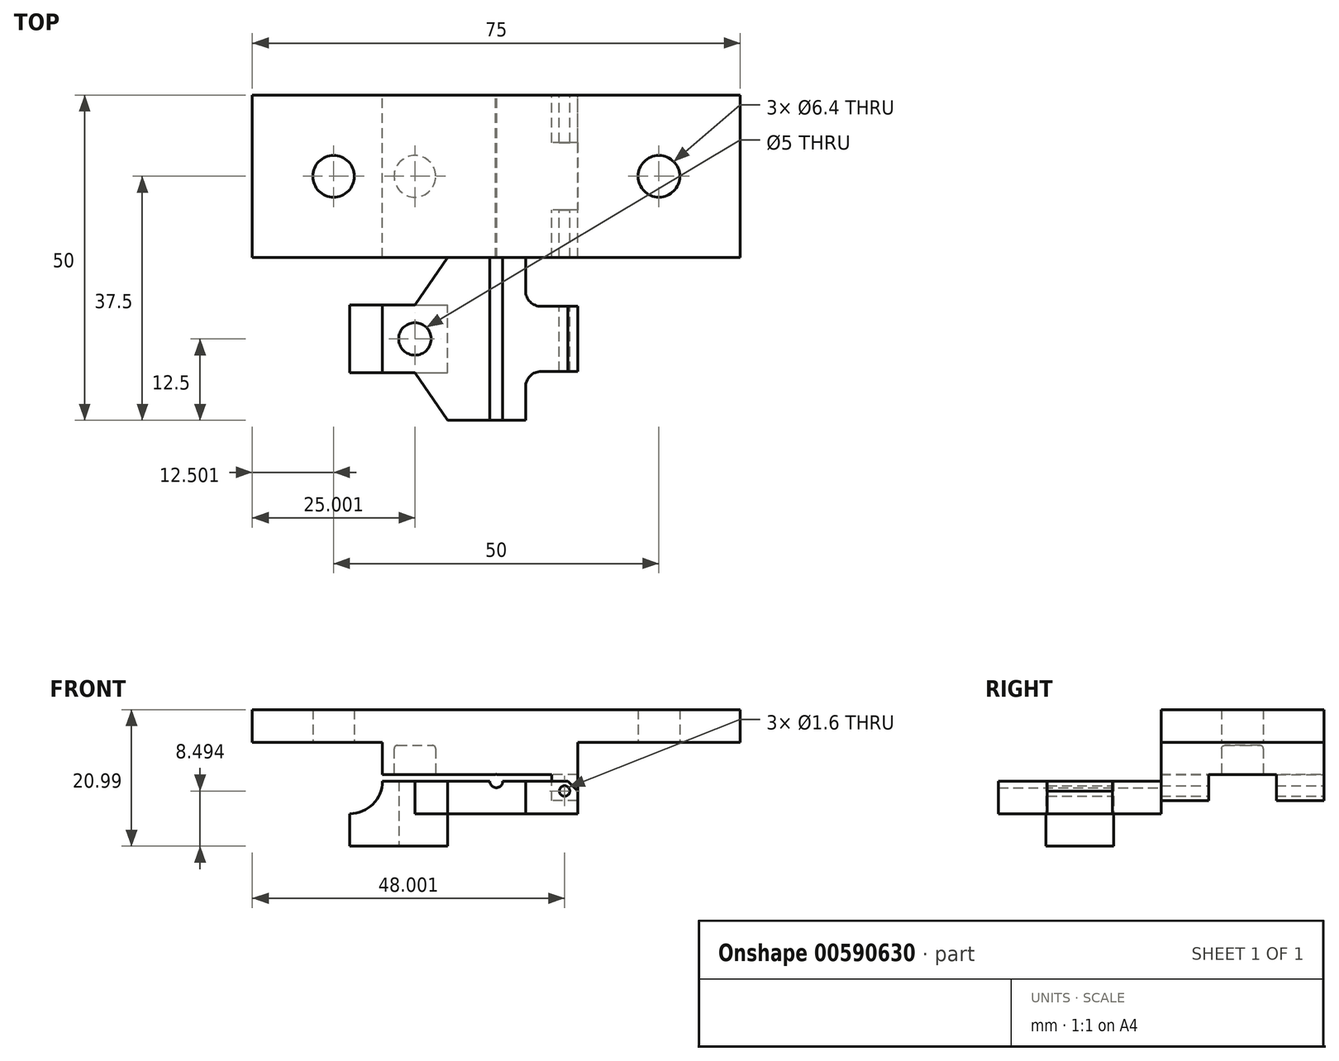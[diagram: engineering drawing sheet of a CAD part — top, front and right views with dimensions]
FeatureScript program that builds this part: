
annotation { "Feature Type Name" : "Feature", "Feature Type Description" : "" }
export const myFeature = defineFeature(function(context is Context, id is Id, definition is map)
    precondition{}
    {
        {
            var Q0;
            Q0=qCreatedBy(makeId("Front.planeOp"),FACE);
            var sketch = newSketch(context, id + "F0", { "sketchPlane" : qUnion([Q0])});
            skLineSegment(sketch, "E0", {"start": v(14.18, -10.49) * mm, "end": v(5.79, -10.49) * mm});
            skLineSegment(sketch, "E1", {"start": v(5.79, -10.49) * mm, "end": v(5.7, -10.4) * mm});
            skArc(sketch, "E2", {"start": v(5.7, -10.4) * mm, "mid": v(5.68, -10.4) * mm, "end": v(5.66, -10.4) * mm});
            skLineSegment(sketch, "E3", {"start": v(5.66, -10.4) * mm, "end": v(5.57, -10.49) * mm});
            skLineSegment(sketch, "E4", {"start": v(5.57, -10.49) * mm, "end": v(-11.82, -10.49) * mm});
            skLineSegment(sketch, "E5", {"start": v(-11.82, -10.49) * mm, "end": v(-11.82, -5.49) * mm});
            skLineSegment(sketch, "E6", {"start": v(-11.82, -5.49) * mm, "end": v(18.18, -5.49) * mm});
            skLineSegment(sketch, "E7", {"start": v(18.18, -5.49) * mm, "end": v(18.18, -14.49) * mm});
            skLineSegment(sketch, "E8", {"start": v(18.18, -14.49) * mm, "end": v(14.18, -14.49) * mm});
            skLineSegment(sketch, "E9", {"start": v(14.18, -14.49) * mm, "end": v(14.18, -10.49) * mm});
            skCircle(sketch, "E10", {"center": v(16.18, -12.99) * mm, "radius": 0.8 * mm});
            skLineSegment(sketch, "E11", {"start": v(5.7, -10.4) * mm, "end": v(5.66, -10.4) * mm, "construction": true});
            skLineSegment(sketch, "E12", {"start": v(18.18, -12.99) * mm, "end": v(14.18, -12.99) * mm, "construction": true});
            skSolve(sketch);
        }
        {
            var Q0;
            Q0 = qSketchRegion(id + "F0", true);
            extrude(context, id + "F1", {"entities" : qUnion([Q0]), "depth" : 25 * mm, "offsetDistance" : 25 * mm});
        }
        {
            var Q0;
            Q0=makeQuery(id+"F1.opExtrude","SWEPT_FACE",FACE,{"disambiguationData":[OSD([sQuery(id+"F0.wireOp",EDGE,"E4")])]});
            var sketch = newSketch(context, id + "F2", { "sketchPlane" : qUnion([Q0])});
            skCircle(sketch, "E13", {"center": v(-6.82, 12.5) * mm, "radius": 3.2 * mm});
            skLineSegment(sketch, "E14", {"start": v(-6.82, 25) * mm, "end": v(-6.82, 0) * mm, "construction": true});
            skSolve(sketch);
        }
        {
            var Q0;
            Q0 = qSketchRegion(id + "F2", true);
            extrude(context, id + "F3", {"entities" : qUnion([Q0]), "operationType" : NewBodyOperationType.REMOVE, "oppositeDirection" : true, "depth" : 4.5 * mm, "offsetDistance" : 25 * mm});
        }
        {
            var Q0;
            Q0=makeQuery(id+"F1.opExtrude","SWEPT_FACE",FACE,{"disambiguationData":[OSD([sQuery(id+"F0.wireOp",EDGE,"E6")])]});
            var sketch = newSketch(context, id + "F4", { "sketchPlane" : qUnion([Q0])});
            skLineSegment(sketch, "E15.bottom", {"start": v(-31.82, -25) * mm, "end": v(43.18, -25) * mm});
            skLineSegment(sketch, "E15.top", {"start": v(-31.82, 0) * mm, "end": v(43.18, 0) * mm});
            skLineSegment(sketch, "E15.left", {"start": v(-31.82, -25) * mm, "end": v(-31.82, 0) * mm});
            skLineSegment(sketch, "E15.right", {"start": v(43.18, -25) * mm, "end": v(43.18, 0) * mm});
            skPoint(sketch, "E16", {"position": v(5.68, 0) * mm});
            skCircle(sketch, "E17", {"center": v(30.68, -12.5) * mm, "radius": 3.2 * mm});
            skLineSegment(sketch, "E18", {"start": v(30.68, 0) * mm, "end": v(30.68, -25) * mm, "construction": true});
            skCircle(sketch, "E19", {"center": v(-19.32, -12.5) * mm, "radius": 3.2 * mm});
            skLineSegment(sketch, "E20", {"start": v(-19.32, -12.5) * mm, "end": v(30.68, -12.5) * mm, "construction": true});
            skSolve(sketch);
        }
        {
            var Q0;
            Q0 = qSketchRegion(id + "F4", true);
            extrude(context, id + "F5", {"entities" : qUnion([Q0]), "operationType" : NewBodyOperationType.ADD, "depth" : 5 * mm, "offsetDistance" : 25 * mm});
        }
        {
            var Q0;
            Q0=makeQuery(id+"F1.opExtrude","SWEPT_FACE",FACE,{"disambiguationData":[OSD([sQuery(id+"F0.wireOp",EDGE,"E9")])]});
            var sketch = newSketch(context, id + "F6", { "sketchPlane" : qUnion([Q0])});
            skLineSegment(sketch, "E21.bottom", {"start": v(7.3, -14.49) * mm, "end": v(17.7, -14.49) * mm});
            skLineSegment(sketch, "E21.top", {"start": v(7.3, -10.49) * mm, "end": v(17.7, -10.49) * mm});
            skLineSegment(sketch, "E21.left", {"start": v(7.3, -14.49) * mm, "end": v(7.3, -10.49) * mm});
            skLineSegment(sketch, "E21.right", {"start": v(17.7, -14.49) * mm, "end": v(17.7, -10.49) * mm});
            skSolve(sketch);
        }
        {
            var Q0;
            Q0 = qSketchRegion(id + "F6", true);
            extrude(context, id + "F7", {"entities" : qUnion([Q0]), "operationType" : NewBodyOperationType.REMOVE, "oppositeDirection" : true, "depth" : 25 * mm, "offsetDistance" : 25 * mm});
        }
        {
            var Q0;
            Q0=makeQuery(id+"F5.boolean.opBoolean","MERGE",FACE,{"derivedFrom":[makeQuery(id+"F1.opExtrude","CAP_FACE",FACE,{"disambiguationData":[OSD([sQuery(id+"F0.wireOp",EDGE,"E0"),sQuery(id+"F0.wireOp",EDGE,"E1"),sQuery(id+"F0.wireOp",EDGE,"E2"),sQuery(id+"F0.wireOp",EDGE,"E3"),sQuery(id+"F0.wireOp",EDGE,"E4"),sQuery(id+"F0.wireOp",EDGE,"E5"),sQuery(id+"F0.wireOp",EDGE,"E6"),sQuery(id+"F0.wireOp",EDGE,"E7"),sQuery(id+"F0.wireOp",EDGE,"E8"),sQuery(id+"F0.wireOp",EDGE,"E9"),sQuery(id+"F0.wireOp",EDGE,"E10")])],"isStart":false}),makeQuery(id+"F5.opExtrude","SWEPT_FACE",FACE,{"disambiguationData":[OSD([sQuery(id+"F4.wireOp",EDGE,"E15.bottom")])]})]});
            var sketch = newSketch(context, id + "F8", { "sketchPlane" : qUnion([Q0])});
            skArc(sketch, "E22", {"start": v(4.68, -11.48) * mm, "mid": v(5.68, -12.48) * mm, "end": v(6.68, -11.48) * mm});
            skLineSegment(sketch, "E23", {"start": v(4.68, -11.48) * mm, "end": v(-11.82, -11.48) * mm});
            skArc(sketch, "E24", {"start": v(-16.82, -16.48) * mm, "mid": v(-13.28, -15.02) * mm, "end": v(-11.82, -11.48) * mm});
            skLineSegment(sketch, "E25", {"start": v(-16.82, -16.48) * mm, "end": v(-16.82, -21.48) * mm});
            skLineSegment(sketch, "E26", {"start": v(-16.82, -21.48) * mm, "end": v(-1.82, -21.48) * mm});
            skLineSegment(sketch, "E27", {"start": v(-1.82, -21.48) * mm, "end": v(-1.82, -16.5) * mm});
            skLineSegment(sketch, "E28", {"start": v(-1.82, -16.5) * mm, "end": v(18.18, -16.5) * mm});
            skCircle(sketch, "E29", {"center": v(5.68, -11.48) * mm, "radius": 1 * mm, "construction": true});
            skPoint(sketch, "E30", {"position": v(5.68, -10.42) * mm});
            skLineSegment(sketch, "E31", {"start": v(5.68, -11.48) * mm, "end": v(5.68, -10.42) * mm, "construction": true});
            skPoint(sketch, "E32", {"position": v(-6.82, -21.48) * mm});
            skLineSegment(sketch, "E33", {"start": v(-11.82, -21.48) * mm, "end": v(-11.82, -11.48) * mm, "construction": true});
            skCircle(sketch, "E34", {"center": v(16.18, -12.99) * mm, "radius": 0.8 * mm});
            skLineSegment(sketch, "E35", {"start": v(18.18, -16.5) * mm, "end": v(18.18, -12.99) * mm});
            skLineSegment(sketch, "E36", {"start": v(18.18, -12.99) * mm, "end": v(16.68, -11.48) * mm});
            skLineSegment(sketch, "E37", {"start": v(16.68, -11.48) * mm, "end": v(6.68, -11.48) * mm});
            skSolve(sketch);
        }
        {
            var Q0;
            Q0 = qSketchRegion(id + "F8", true);
            extrude(context, id + "F9", {"entities" : qUnion([Q0]), "depth" : 25 * mm, "offsetDistance" : 25 * mm});
        }
        {
            var Q0;
            Q0=makeQuery(id+"F9.opExtrude","SWEPT_FACE",FACE,{"disambiguationData":[OSD([sQuery(id+"F8.wireOp",EDGE,"E28")])]});
            var sketch = newSketch(context, id + "F10", { "sketchPlane" : qUnion([Q0])});
            skLineSegment(sketch, "E38", {"start": v(18.18, 42.5) * mm, "end": v(12.58, 42.5) * mm});
            skArc(sketch, "E39", {"start": v(10.18, 44.9) * mm, "mid": v(10.88, 43.2) * mm, "end": v(12.58, 42.5) * mm});
            skLineSegment(sketch, "E40", {"start": v(10.18, 44.9) * mm, "end": v(10.18, 50) * mm});
            skLineSegment(sketch, "E41", {"start": v(10.18, 50) * mm, "end": v(18.18, 50) * mm});
            skLineSegment(sketch, "E42", {"start": v(18.18, 50) * mm, "end": v(18.18, 42.5) * mm});
            skLineSegment(sketch, "E43", {"start": v(18.18, 37.5) * mm, "end": v(13.45, 37.5) * mm, "construction": true});
            skLineSegment(sketch, "E44.MirrorCS", {"start": v(18.18, 32.5) * mm, "end": v(12.58, 32.5) * mm});
            skArc(sketch, "E45.MirrorCS", {"start": v(10.18, 30.1) * mm, "mid": v(10.88, 31.8) * mm, "end": v(12.58, 32.5) * mm});
            skLineSegment(sketch, "E46.MirrorCS", {"start": v(10.18, 30.1) * mm, "end": v(10.18, 25) * mm});
            skLineSegment(sketch, "E47.MirrorCS", {"start": v(10.18, 25) * mm, "end": v(18.18, 25) * mm});
            skLineSegment(sketch, "E48.MirrorCS", {"start": v(18.18, 25) * mm, "end": v(18.18, 32.5) * mm});
            skSolve(sketch);
        }
        {
            var Q0;
            Q0 = qSketchRegion(id + "F10", true);
            extrude(context, id + "F11", {"entities" : qUnion([Q0]), "operationType" : NewBodyOperationType.REMOVE, "endBound" : BoundingType.UP_TO_NEXT, "oppositeDirection" : true, "depth" : 25 * mm, "offsetDistance" : 25 * mm});
        }
        {
            var Q0;
            Q0=makeQuery(id+"F9.opExtrude","SWEPT_FACE",FACE,{"disambiguationData":[OSD([sQuery(id+"F8.wireOp",EDGE,"E26")])]});
            var sketch = newSketch(context, id + "F12", { "sketchPlane" : qUnion([Q0])});
            skLineSegment(sketch, "E49", {"start": v(-6.82, 54.17) * mm, "end": v(-6.82, 20.83) * mm, "construction": true});
            skPoint(sketch, "E50", {"position": v(-6.82, 37.5) * mm});
            skSolve(sketch);
        }
        {
            var Q0;
            Q0=sQuery(id+"F12.wireOp",VERTEX,"E50");
            var Q1;
            Q1=makeQuery(id+"F9.opExtrude","SWEPT_BODY",BODY,{"disambiguationData":[OSD([sQuery(id+"F8.wireOp",EDGE,"NBDfFKbi-qGs6-JKBK-J2hD-w34obwZNQX4o"),sQuery(id+"F8.wireOp",EDGE,"E22"),sQuery(id+"F8.wireOp",EDGE,"E23"),sQuery(id+"F8.wireOp",EDGE,"E24"),sQuery(id+"F8.wireOp",EDGE,"E25"),sQuery(id+"F8.wireOp",EDGE,"E26"),sQuery(id+"F8.wireOp",EDGE,"E27"),sQuery(id+"F8.wireOp",EDGE,"E28"),sQuery(id+"F8.wireOp",EDGE,"RzoUX08u-rRmn-cew6-mJfb-Ws3PqcxDGY6H")])]});
            hole(context, id + "F13", {"style" : HoleStyle.SIMPLE, "endStyle" : HoleEndStyle.THROUGH, "standardTappedOrClearance" : lookupTablePath({ "standard" : "ISO", "engagement" : "75%", "pitch" : "1 mm", "size" : "M6", "type" : "Tapped" }), "standardBlindInLast" : lookupTablePath({ "standard" : "ISO", "engagement" : "75%", "pitch" : "1 mm", "size" : "M6", "type" : "Tapped" }), "holeDiameter" : 5 * mm, "majorDiameter" : 6 * mm, "showTappedDepth" : true, "isTappedThrough" : true, "tappedDepth" : 12 * mm, "tapClearance" : 3, "locations" : qUnion([Q0]), "scope" : qUnion([Q1])});
        }
        {
            var Q0;
            Q0=makeQuery(id+"F9.opExtrude","SWEPT_FACE",FACE,{"disambiguationData":[OSD([sQuery(id+"F8.wireOp",EDGE,"E27")])]});
            var sketch = newSketch(context, id + "F14", { "sketchPlane" : qUnion([Q0])});
            skLineSegment(sketch, "E51.bottom", {"start": v(-25, -21.48) * mm, "end": v(-32.3, -21.48) * mm});
            skLineSegment(sketch, "E51.top", {"start": v(-25, -16.5) * mm, "end": v(-32.3, -16.5) * mm});
            skLineSegment(sketch, "E51.left", {"start": v(-25, -21.48) * mm, "end": v(-25, -16.5) * mm});
            skLineSegment(sketch, "E51.right", {"start": v(-32.3, -21.48) * mm, "end": v(-32.3, -16.5) * mm});
            skLineSegment(sketch, "E52.bottom", {"start": v(-50, -21.48) * mm, "end": v(-42.7, -21.48) * mm});
            skLineSegment(sketch, "E52.top", {"start": v(-50, -16.5) * mm, "end": v(-42.7, -16.5) * mm});
            skLineSegment(sketch, "E52.left", {"start": v(-50, -21.48) * mm, "end": v(-50, -16.5) * mm});
            skLineSegment(sketch, "E52.right", {"start": v(-42.7, -21.48) * mm, "end": v(-42.7, -16.5) * mm});
            skSolve(sketch);
        }
        {
            var Q0;
            Q0 = qSketchRegion(id + "F14", true);
            extrude(context, id + "F15", {"entities" : qUnion([Q0]), "operationType" : NewBodyOperationType.REMOVE, "oppositeDirection" : true, "depth" : 25 * mm, "offsetDistance" : 25 * mm});
        }
        {
            var Q0;
            Q0=makeQuery(id+"F15.boolean.opBoolean","MERGE",FACE,{"derivedFrom":[makeQuery(id+"F9.opExtrude","SWEPT_FACE",FACE,{"disambiguationData":[OSD([sQuery(id+"F8.wireOp",EDGE,"E28")])]}),makeQuery(id+"F15.opExtrude","SWEPT_FACE",FACE,{"disambiguationData":[OSD([sQuery(id+"F14.wireOp",EDGE,"E51.top")])]}),makeQuery(id+"F15.opExtrude","SWEPT_FACE",FACE,{"disambiguationData":[OSD([sQuery(id+"F14.wireOp",EDGE,"E52.top")])]})]});
            var sketch = newSketch(context, id + "F16", { "sketchPlane" : qUnion([Q0])});
            skLineSegment(sketch, "E53", {"start": v(-16.82, 42.7) * mm, "end": v(-6.82, 42.7) * mm});
            skLineSegment(sketch, "E54", {"start": v(-6.82, 42.7) * mm, "end": v(-1.82, 50) * mm});
            skLineSegment(sketch, "E55", {"start": v(-1.82, 50) * mm, "end": v(-16.82, 50) * mm});
            skLineSegment(sketch, "E56", {"start": v(-16.82, 50) * mm, "end": v(-16.82, 42.7) * mm});
            skPoint(sketch, "E57", {"position": v(-6.82, 37.5) * mm});
            skLineSegment(sketch, "E58", {"start": v(-6.82, 37.5) * mm, "end": v(-6.82, 42.7) * mm, "construction": true});
            skLineSegment(sketch, "E59", {"start": v(-6.82, 37.5) * mm, "end": v(-24.14, 37.5) * mm, "construction": true});
            skLineSegment(sketch, "E60.MirrorCS", {"start": v(-16.82, 32.3) * mm, "end": v(-6.82, 32.3) * mm});
            skLineSegment(sketch, "E61.MirrorCS", {"start": v(-6.82, 32.3) * mm, "end": v(-1.82, 25) * mm});
            skLineSegment(sketch, "E62.MirrorCS", {"start": v(-16.82, 25) * mm, "end": v(-16.82, 32.3) * mm});
            skLineSegment(sketch, "E63.MirrorCS", {"start": v(-1.82, 25) * mm, "end": v(-16.82, 25) * mm});
            skSolve(sketch);
        }
        {
            var Q0;
            Q0 = qSketchRegion(id + "F16", true);
            var Q1;
            Q1 = qConstructionFilter(qBodyType(qCreatedBy(id + "F16" ,EDGE), BodyType.WIRE), ConstructionObject.NO);
            extrude(context, id + "F17", {"entities" : qUnion([Q0]), "operationType" : NewBodyOperationType.REMOVE, "surfaceEntities" : qUnion([Q1]), "endBound" : BoundingType.UP_TO_NEXT, "oppositeDirection" : true, "depth" : 25 * mm, "offsetDistance" : 25 * mm});
        }
        {
            var Q0;
            Q0=makeQuery(id+"F3.boolean.opBoolean","COPY",FACE,{"derivedFrom":makeQuery(id+"F3.opExtrude","CAP_FACE",FACE,{"disambiguationData":[OSD([sQuery(id+"F2.wireOp",EDGE,"E13")])],"isStart":false})});
            fillet(context, id + "F18", {"entities" : qUnion([Q0]), "radius" : 0.5 * mm, "tangentPropagation" : true, "allowEdgeOverflow" : false});
        }
    });
